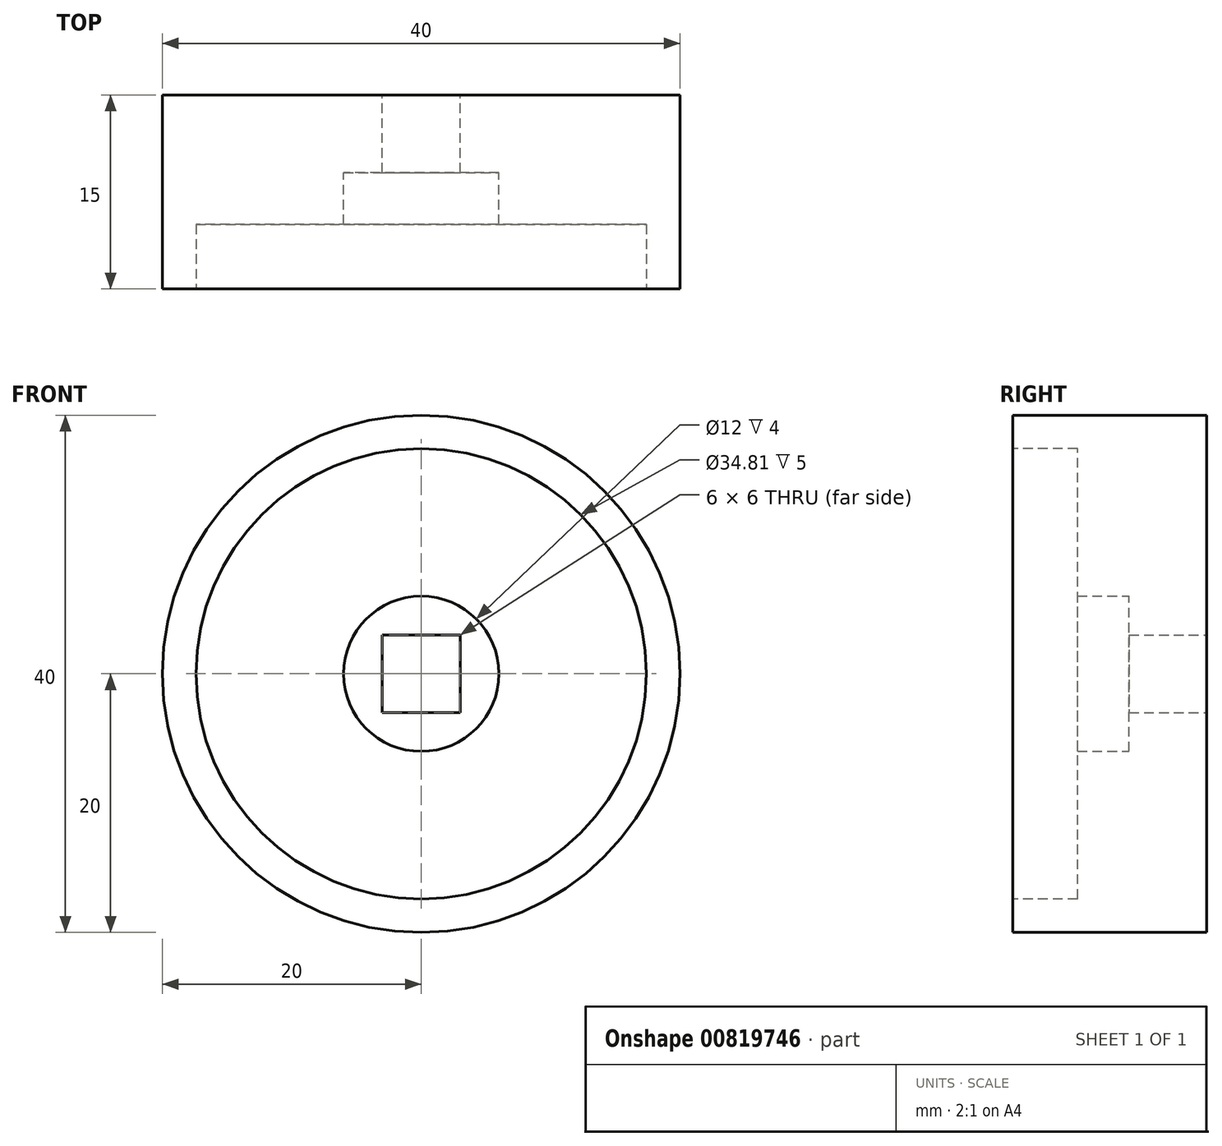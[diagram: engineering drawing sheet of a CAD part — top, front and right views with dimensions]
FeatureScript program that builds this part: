
annotation { "Feature Type Name" : "Feature", "Feature Type Description" : "" }
export const myFeature = defineFeature(function(context is Context, id is Id, definition is map)
    precondition{}
    {
        {
            var Q0;
            Q0=qCreatedBy(makeId("Front.planeOp"),FACE);
            var sketch = newSketch(context, id + "F0", { "sketchPlane" : qUnion([Q0])});
            skCircle(sketch, "E0", {"center": v(0, 0) * mm, "radius": 20 * mm});
            skLineSegment(sketch, "E1.bottom", {"start": v(-3, 3) * mm, "end": v(3, 3) * mm});
            skLineSegment(sketch, "E1.top", {"start": v(-3, -3) * mm, "end": v(3, -3) * mm});
            skLineSegment(sketch, "E1.left", {"start": v(-3, 3) * mm, "end": v(-3, -3) * mm});
            skLineSegment(sketch, "E1.right", {"start": v(3, 3) * mm, "end": v(3, -3) * mm});
            skCircle(sketch, "E2", {"center": v(0, 0) * mm, "radius": 6 * mm});
            skCircle(sketch, "E3", {"center": v(0, 0) * mm, "radius": 17.23 * mm});
            skSolve(sketch);
        }
        {
            var Q0;
            Q0=makeQuery(id+"F0.imprint","IMPRINT",FACE,{"disambiguationData":[TD([[makeQuery(id+"F0.imprint","IMPRINT",EDGE,{"derivedFrom":sQuery(id+"F0.wireOp",EDGE,"E1.bottom")}),1.0]])]});
            extrude(context, id + "F1", {"entities" : qUnion([Q0]), "depth" : 6 * mm, "offsetDistance" : 25 * mm});
        }
        {
            var Q0;
            Q0=makeQuery(id+"F0.imprint","IMPRINT",FACE,{"disambiguationData":[TD([[makeQuery(id+"F0.imprint","IMPRINT",EDGE,{"derivedFrom":sQuery(id+"F0.wireOp",EDGE,"E2")}),-1.0]])]});
            extrude(context, id + "F2", {"entities" : qUnion([Q0]), "operationType" : NewBodyOperationType.ADD, "depth" : 5 * mm, "offsetDistance" : 25 * mm});
        }
        {
            var Q0;
            Q0=makeQuery(id+"F0.imprint","IMPRINT",FACE,{"disambiguationData":[TD([[makeQuery(id+"F0.imprint","IMPRINT",EDGE,{"derivedFrom":sQuery(id+"F0.wireOp",EDGE,"E1.bottom")}),1.0]])]});
            extrude(context, id + "F3", {"entities" : qUnion([Q0]), "operationType" : NewBodyOperationType.ADD, "depth" : 5 * mm, "offsetDistance" : 25 * mm});
        }
        {
            var Q0;
            Q0=makeQuery(id+"F0.imprint","IMPRINT",FACE,{"disambiguationData":[TD([[makeQuery(id+"F0.imprint","IMPRINT",EDGE,{"derivedFrom":sQuery(id+"F0.wireOp",EDGE,"E2")}),-1.0]])]});
            var Q1;
            Q1=makeQuery(id+"F0.imprint","IMPRINT",FACE,{"disambiguationData":[TD([[makeQuery(id+"F0.imprint","IMPRINT",EDGE,{"derivedFrom":sQuery(id+"F0.wireOp",EDGE,"E0")}),1.0]])]});
            extrude(context, id + "F4", {"entities" : qUnion([Q0, Q1]), "operationType" : NewBodyOperationType.ADD, "depth" : 15 * mm, "offsetDistance" : 25 * mm});
        }
        {
            var Q0;
            Q0=makeQuery(id+"F4.opExtrude","CAP_FACE",FACE,{"disambiguationData":[OSD([sQuery(id+"F0.wireOp",EDGE,"E0"),sQuery(id+"F0.wireOp",EDGE,"E2")])],"isStart":false});
            var sketch = newSketch(context, id + "F5", { "sketchPlane" : qUnion([Q0])});
            skCircle(sketch, "E4", {"center": v(0, 0) * mm, "radius": 17.4 * mm});
            skSolve(sketch);
        }
        {
            var Q0;
            Q0=makeQuery(id+"F5.imprint","IMPRINT",FACE,{"disambiguationData":[TD([[makeQuery(id+"F5.imprint","IMPRINT",EDGE,{"derivedFrom":sQuery(id+"F5.wireOp",EDGE,"E4")}),1.0]])]});
            extrude(context, id + "F6", {"entities" : qUnion([Q0]), "operationType" : NewBodyOperationType.REMOVE, "oppositeDirection" : true, "depth" : 5 * mm, "offsetDistance" : 25 * mm});
        }
    });
